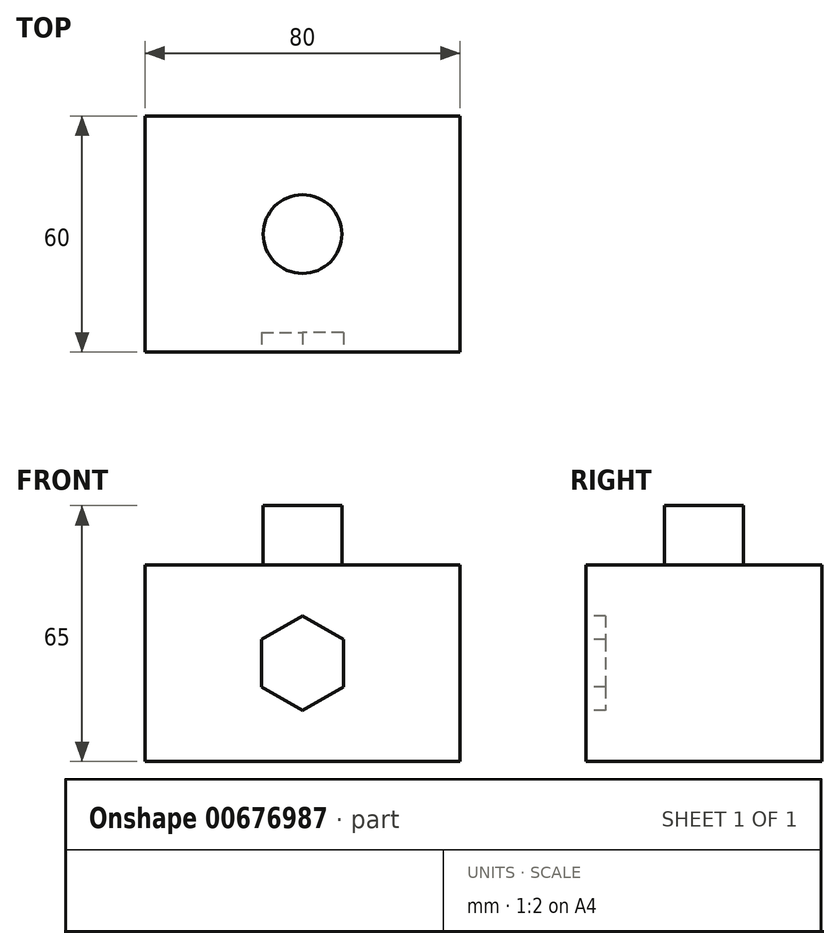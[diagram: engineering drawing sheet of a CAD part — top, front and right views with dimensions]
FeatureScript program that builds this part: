
annotation { "Feature Type Name" : "Feature", "Feature Type Description" : "" }
export const myFeature = defineFeature(function(context is Context, id is Id, definition is map)
    precondition{}
    {
        {
            var Q0;
            Q0=qCreatedBy(makeId("Top.planeOp"),FACE);
            var sketch = newSketch(context, id + "F0", { "sketchPlane" : qUnion([Q0])});
            skLineSegment(sketch, "E0.bottom", {"start": v(40, 30) * mm, "end": v(-40, 30) * mm});
            skLineSegment(sketch, "E0.top", {"start": v(40, -30) * mm, "end": v(-40, -30) * mm});
            skLineSegment(sketch, "E0.left", {"start": v(40, 30) * mm, "end": v(40, -30) * mm});
            skLineSegment(sketch, "E0.right", {"start": v(-40, 30) * mm, "end": v(-40, -30) * mm});
            skPoint(sketch, "E0.middle", {"position": v(0, 0) * mm});
            skSolve(sketch);
        }
        {
            var Q0;
            Q0 = qSketchRegion(id + "F0", true);
            extrude(context, id + "F1", {"entities" : qUnion([Q0]), "depth" : 50 * mm, "offsetDistance" : 25 * mm});
        }
        {
            var Q0;
            Q0=makeQuery(id+"F1.opExtrude","CAP_FACE",FACE,{"disambiguationData":[OSD([sQuery(id+"F0.wireOp",EDGE,"E0.bottom"),sQuery(id+"F0.wireOp",EDGE,"E0.top"),sQuery(id+"F0.wireOp",EDGE,"E0.left"),sQuery(id+"F0.wireOp",EDGE,"E0.right")])],"isStart":false});
            var sketch = newSketch(context, id + "F2", { "sketchPlane" : qUnion([Q0])});
            skCircle(sketch, "E1", {"center": v(0, 0) * mm, "radius": 10 * mm});
            skSolve(sketch);
        }
        {
            var Q0;
            Q0 = qSketchRegion(id + "F2", true);
            extrude(context, id + "F3", {"entities" : qUnion([Q0]), "operationType" : NewBodyOperationType.ADD, "depth" : 15 * mm, "offsetDistance" : 25 * mm});
        }
        {
            var Q0;
            Q0=makeQuery(id+"F1.opExtrude","SWEPT_FACE",FACE,{"disambiguationData":[OSD([sQuery(id+"F0.wireOp",EDGE,"E0.top")])]});
            var sketch = newSketch(context, id + "F4", { "sketchPlane" : qUnion([Q0])});
            skCircle(sketch, "E2.cCircle", {"center": v(0, 25) * mm, "radius": 10.4 * mm, "construction": true});
            skLineSegment(sketch, "E2.0", {"start": v(10.4, 19) * mm, "end": v(0, 13) * mm});
            skLineSegment(sketch, "E2.1", {"start": v(0, 13) * mm, "end": v(-10.4, 19) * mm});
            skLineSegment(sketch, "E2.2", {"start": v(-10.4, 19) * mm, "end": v(-10.4, 31) * mm});
            skLineSegment(sketch, "E2.3", {"start": v(-10.4, 31) * mm, "end": v(0, 37) * mm});
            skLineSegment(sketch, "E2.4", {"start": v(0, 37) * mm, "end": v(10.4, 31) * mm});
            skLineSegment(sketch, "E2.5", {"start": v(10.4, 31) * mm, "end": v(10.4, 19) * mm});
            skPoint(sketch, "E2.0.midPoint", {"position": v(5.2, 16) * mm});
            skSolve(sketch);
        }
        {
            var Q0;
            Q0 = qSketchRegion(id + "F4", true);
            extrude(context, id + "F5", {"entities" : qUnion([Q0]), "operationType" : NewBodyOperationType.REMOVE, "oppositeDirection" : true, "depth" : 5 * mm, "offsetDistance" : 25 * mm});
        }
    });
